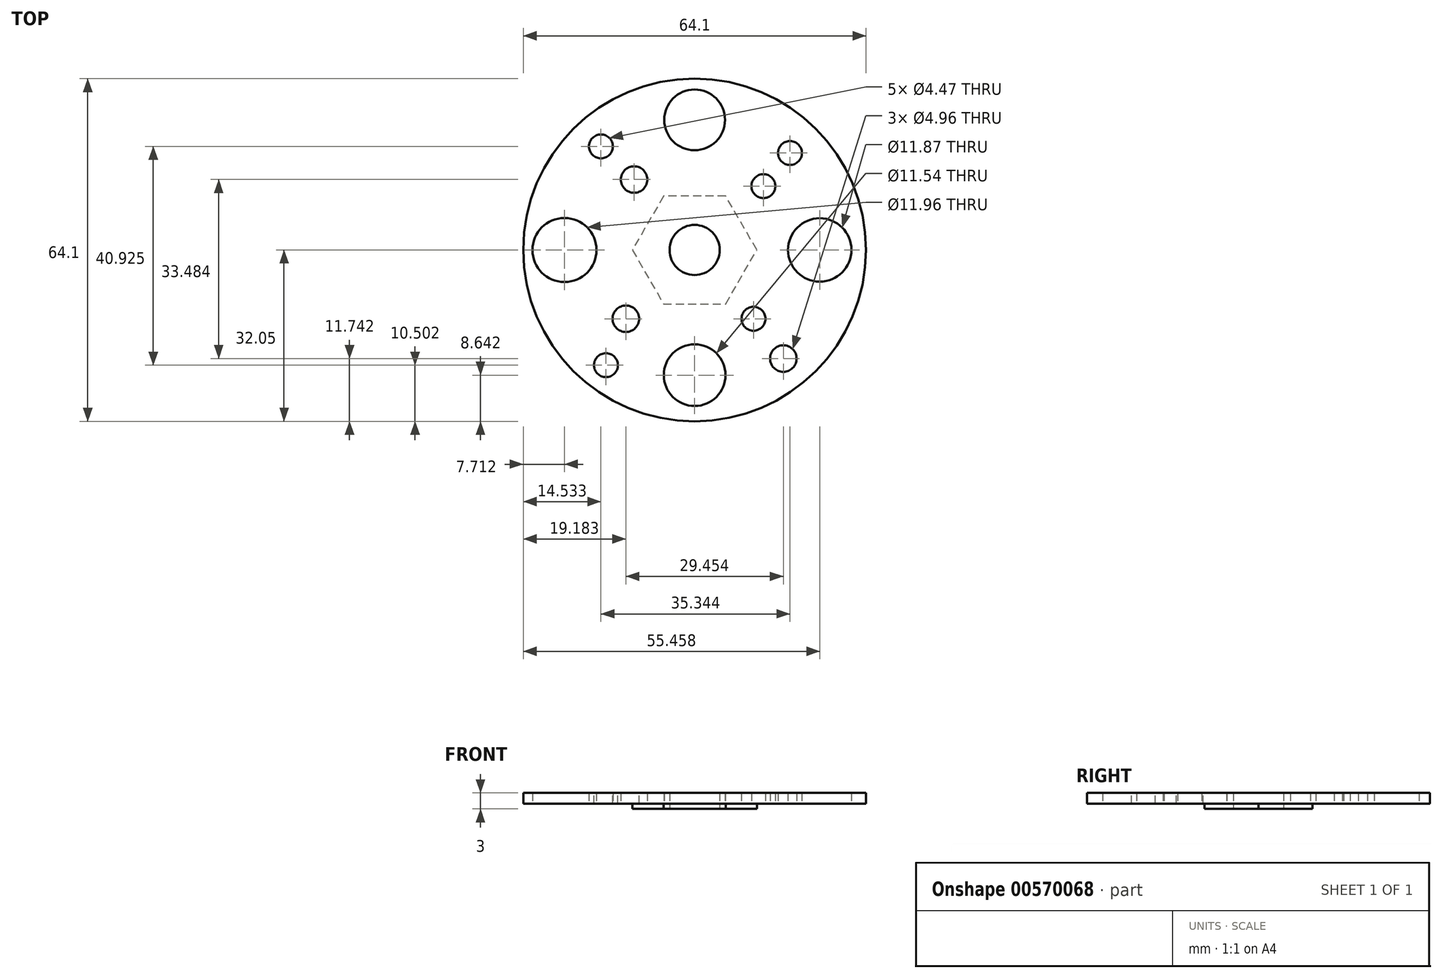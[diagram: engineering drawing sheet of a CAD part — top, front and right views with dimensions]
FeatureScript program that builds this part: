
annotation { "Feature Type Name" : "Feature", "Feature Type Description" : "" }
export const myFeature = defineFeature(function(context is Context, id is Id, definition is map)
    precondition{}
    {
        {
            var Q0;
            Q0=qCreatedBy(makeId("Top.planeOp"),FACE);
            var sketch = newSketch(context, id + "F0", { "sketchPlane" : qUnion([Q0])});
            skCircle(sketch, "E0", {"center": v(0, 0) * mm, "radius": 32.05 * mm});
            skSolve(sketch);
        }
        {
            var Q0;
            Q0=makeQuery(id+"F0.imprint","IMPRINT",FACE,{"disambiguationData":[TD([[makeQuery(id+"F0.imprint","IMPRINT",EDGE,{"derivedFrom":sQuery(id+"F0.wireOp",EDGE,"E0")}),1.0]])]});
            extrude(context, id + "F1", {"entities" : qUnion([Q0]), "oppositeDirection" : true, "depth" : 2 * mm, "offsetDistance" : 25.4 * mm});
        }
        {
            var Q0;
            Q0=makeQuery(id+"F1.opExtrude","CAP_FACE",FACE,{"disambiguationData":[OSD([sQuery(id+"F0.wireOp",EDGE,"E0")])],"isStart":false});
            var sketch = newSketch(context, id + "F2", { "sketchPlane" : qUnion([Q0])});
            skCircle(sketch, "E1", {"center": v(0, -24.34) * mm, "radius": 5.69 * mm});
            skSolve(sketch);
        }
        {
            var Q0;
            Q0 = qSketchRegion(id + "F2", true);
            extrude(context, id + "F3", {"entities" : qUnion([Q0]), "operationType" : NewBodyOperationType.REMOVE, "oppositeDirection" : true, "depth" : 25 * mm, "offsetDistance" : 25 * mm});
        }
        {
            var Q0;
            Q0=makeQuery(id+"F1.opExtrude","CAP_FACE",FACE,{"disambiguationData":[OSD([sQuery(id+"F0.wireOp",EDGE,"E0")])],"isStart":false});
            var sketch = newSketch(context, id + "F4", { "sketchPlane" : qUnion([Q0])});
            skCircle(sketch, "E2", {"center": v(23.4, 0) * mm, "radius": 5.93 * mm});
            skSolve(sketch);
        }
        {
            var Q0;
            Q0 = qSketchRegion(id + "F4", true);
            extrude(context, id + "F5", {"entities" : qUnion([Q0]), "operationType" : NewBodyOperationType.REMOVE, "oppositeDirection" : true, "depth" : 25 * mm, "offsetDistance" : 25 * mm});
        }
        {
            var Q0;
            Q0=makeQuery(id+"F1.opExtrude","CAP_FACE",FACE,{"disambiguationData":[OSD([sQuery(id+"F0.wireOp",EDGE,"E0")])],"isStart":false});
            var sketch = newSketch(context, id + "F6", { "sketchPlane" : qUnion([Q0])});
            skCircle(sketch, "E3", {"center": v(0, 23.4) * mm, "radius": 5.77 * mm});
            skSolve(sketch);
        }
        {
            var Q0;
            Q0 = qSketchRegion(id + "F6", true);
            extrude(context, id + "F7", {"entities" : qUnion([Q0]), "operationType" : NewBodyOperationType.REMOVE, "oppositeDirection" : true, "depth" : 25 * mm, "offsetDistance" : 25 * mm});
        }
        {
            var Q0;
            Q0=makeQuery(id+"F1.opExtrude","CAP_FACE",FACE,{"disambiguationData":[OSD([sQuery(id+"F0.wireOp",EDGE,"E0")])],"isStart":false});
            var sketch = newSketch(context, id + "F8", { "sketchPlane" : qUnion([Q0])});
            skCircle(sketch, "E4", {"center": v(-24.34, 0) * mm, "radius": 5.98 * mm});
            skSolve(sketch);
        }
        {
            var Q0;
            Q0 = qSketchRegion(id + "F8", true);
            extrude(context, id + "F9", {"entities" : qUnion([Q0]), "operationType" : NewBodyOperationType.REMOVE, "oppositeDirection" : true, "depth" : 25 * mm, "offsetDistance" : 25 * mm});
        }
        {
            var Q0;
            Q0=makeQuery(id+"F1.opExtrude","CAP_FACE",FACE,{"disambiguationData":[OSD([sQuery(id+"F0.wireOp",EDGE,"E0")])],"isStart":false});
            var sketch = newSketch(context, id + "F10", { "sketchPlane" : qUnion([Q0])});
            skCircle(sketch, "E5.cCircle", {"center": v(0, 0) * mm, "radius": 10.08 * mm, "construction": true});
            skLineSegment(sketch, "E5.0", {"start": v(5.82, -10.08) * mm, "end": v(-5.82, -10.08) * mm});
            skLineSegment(sketch, "E5.1", {"start": v(-5.82, -10.08) * mm, "end": v(-11.64, 0) * mm});
            skLineSegment(sketch, "E5.2", {"start": v(-11.64, 0) * mm, "end": v(-5.82, 10.08) * mm});
            skLineSegment(sketch, "E5.3", {"start": v(-5.82, 10.08) * mm, "end": v(5.82, 10.08) * mm});
            skLineSegment(sketch, "E5.4", {"start": v(5.82, 10.08) * mm, "end": v(11.64, 0) * mm});
            skLineSegment(sketch, "E5.5", {"start": v(11.64, 0) * mm, "end": v(5.82, -10.08) * mm});
            skPoint(sketch, "E5.0.midPoint", {"position": v(0, -10.08) * mm});
            skSolve(sketch);
        }
        {
            var Q0;
            Q0 = qSketchRegion(id + "F10", true);
            extrude(context, id + "F11", {"entities" : qUnion([Q0]), "operationType" : NewBodyOperationType.ADD, "depth" : 1 * mm, "offsetDistance" : 25 * mm});
        }
        {
            var Q0;
            Q0=makeQuery(id+"F11.opExtrude","CAP_FACE",FACE,{"disambiguationData":[OSD([sQuery(id+"F10.wireOp",EDGE,"E5.0"),sQuery(id+"F10.wireOp",EDGE,"E5.1"),sQuery(id+"F10.wireOp",EDGE,"E5.2"),sQuery(id+"F10.wireOp",EDGE,"E5.3"),sQuery(id+"F10.wireOp",EDGE,"E5.4"),sQuery(id+"F10.wireOp",EDGE,"E5.5")])],"isStart":false});
            var sketch = newSketch(context, id + "F12", { "sketchPlane" : qUnion([Q0])});
            skCircle(sketch, "E6", {"center": v(0, 0) * mm, "radius": 4.69 * mm});
            skSolve(sketch);
        }
        {
            var Q0;
            Q0 = qSketchRegion(id + "F12", true);
            extrude(context, id + "F13", {"entities" : qUnion([Q0]), "operationType" : NewBodyOperationType.REMOVE, "oppositeDirection" : true, "depth" : 25 * mm, "offsetDistance" : 25 * mm});
        }
        {
            var Q0;
            Q0=makeQuery(id+"F1.opExtrude","CAP_FACE",FACE,{"disambiguationData":[OSD([sQuery(id+"F0.wireOp",EDGE,"E0")])],"isStart":false});
            var sketch = newSketch(context, id + "F14", { "sketchPlane" : qUnion([Q0])});
            skCircle(sketch, "E7", {"center": v(-11.32, -13.18) * mm, "radius": 2.48 * mm});
            skCircle(sketch, "E8", {"center": v(-17.52, -19.38) * mm, "radius": 2.24 * mm});
            skSolve(sketch);
        }
        {
            var Q0;
            Q0 = qSketchRegion(id + "F14", true);
            extrude(context, id + "F15", {"entities" : qUnion([Q0]), "operationType" : NewBodyOperationType.REMOVE, "oppositeDirection" : true, "depth" : 25 * mm, "offsetDistance" : 25 * mm});
        }
        {
            var Q0;
            Q0=makeQuery(id+"F1.opExtrude","CAP_FACE",FACE,{"disambiguationData":[OSD([sQuery(id+"F0.wireOp",EDGE,"E0")])],"isStart":false});
            var sketch = newSketch(context, id + "F16", { "sketchPlane" : qUnion([Q0])});
            skCircle(sketch, "E9", {"center": v(12.87, -11.94) * mm, "radius": 2.24 * mm});
            skCircle(sketch, "E10", {"center": v(17.83, -18.14) * mm, "radius": 2.24 * mm});
            skSolve(sketch);
        }
        {
            var Q0;
            Q0 = qSketchRegion(id + "F16", true);
            extrude(context, id + "F17", {"entities" : qUnion([Q0]), "operationType" : NewBodyOperationType.REMOVE, "oppositeDirection" : true, "depth" : 25 * mm, "offsetDistance" : 25 * mm});
        }
        {
            var Q0;
            Q0=makeQuery(id+"F1.opExtrude","CAP_FACE",FACE,{"disambiguationData":[OSD([sQuery(id+"F0.wireOp",EDGE,"E0")])],"isStart":false});
            var sketch = newSketch(context, id + "F18", { "sketchPlane" : qUnion([Q0])});
            skCircle(sketch, "E11", {"center": v(11, 12.87) * mm, "radius": 2.24 * mm});
            skCircle(sketch, "E12", {"center": v(16.59, 20.3) * mm, "radius": 2.48 * mm});
            skSolve(sketch);
        }
        {
            var Q0;
            Q0 = qSketchRegion(id + "F18", true);
            extrude(context, id + "F19", {"entities" : qUnion([Q0]), "operationType" : NewBodyOperationType.REMOVE, "oppositeDirection" : true, "depth" : 25 * mm, "offsetDistance" : 25 * mm});
        }
        {
            var Q0;
            Q0=qCreatedBy(makeId("Top.planeOp"),FACE);
            var sketch = newSketch(context, id + "F20", { "sketchPlane" : qUnion([Q0])});
            skCircle(sketch, "E13", {"center": v(-12.87, -12.87) * mm, "radius": 2.48 * mm});
            skCircle(sketch, "E14", {"center": v(-16.59, -21.55) * mm, "radius": 2.24 * mm});
            skSolve(sketch);
        }
        {
            var Q0;
            Q0 = qSketchRegion(id + "F20", true);
            extrude(context, id + "F21", {"entities" : qUnion([Q0]), "operationType" : NewBodyOperationType.REMOVE, "oppositeDirection" : true, "depth" : 25 * mm, "offsetDistance" : 25 * mm});
        }
    });
